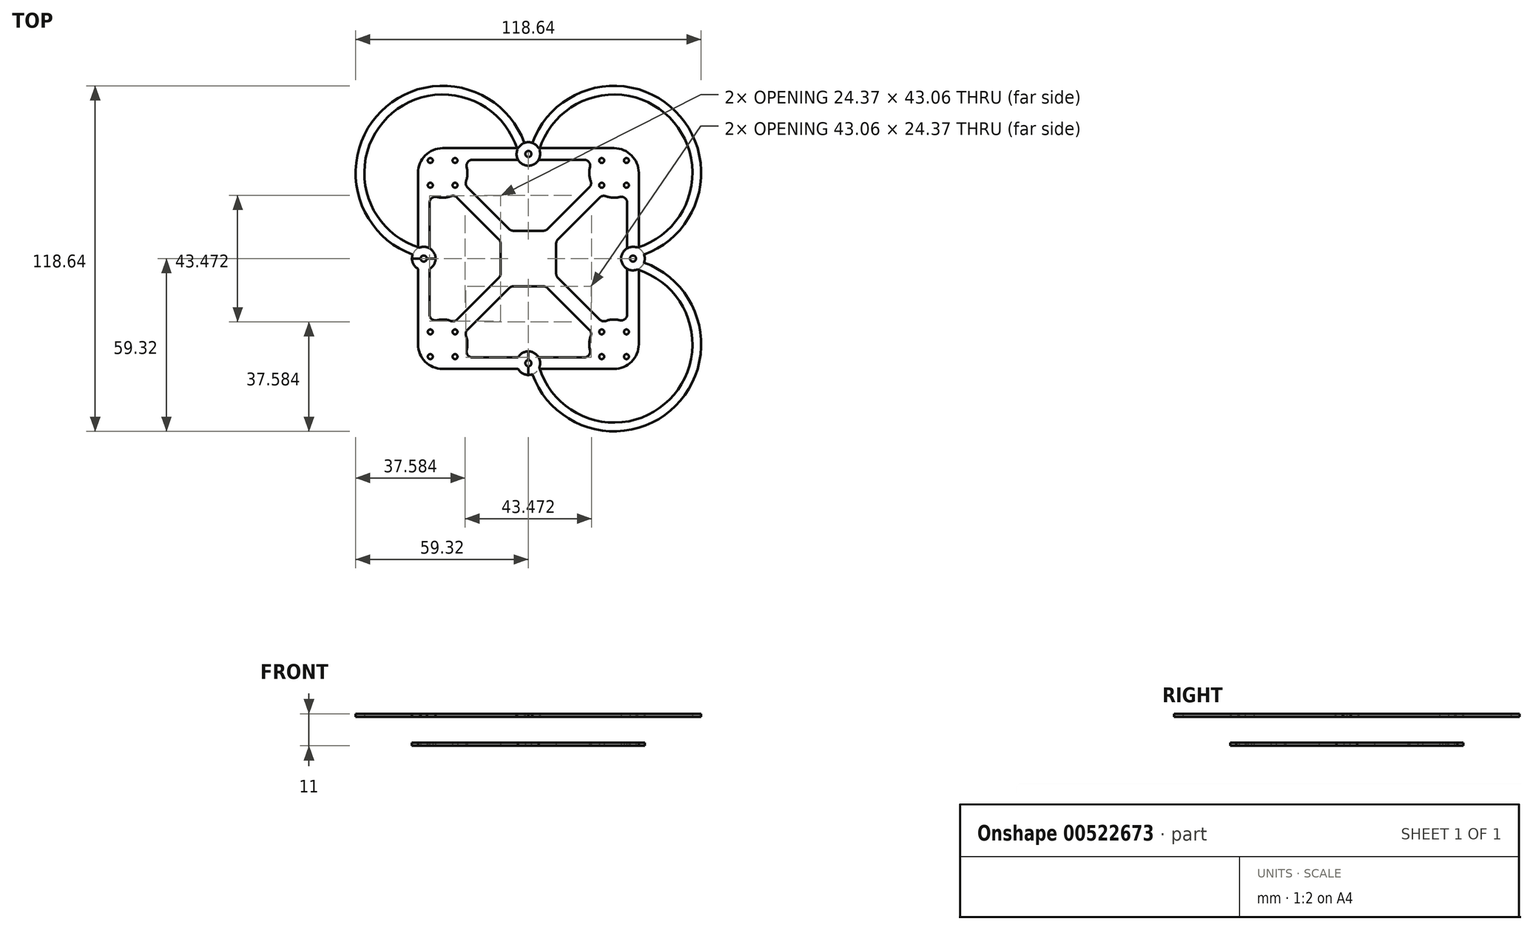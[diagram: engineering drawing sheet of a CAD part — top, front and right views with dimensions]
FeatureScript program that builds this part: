
annotation { "Feature Type Name" : "Feature", "Feature Type Description" : "" }
export const myFeature = defineFeature(function(context is Context, id is Id, definition is map)
    precondition{}
    {
        {
            var Q0;
            Q0=qCreatedBy(makeId("Top.planeOp"),FACE);
            var sketch = newSketch(context, id + "F0", { "sketchPlane" : qUnion([Q0])});
            skCircle(sketch, "E0", {"center": v(0, 0) * mm, "radius": 41.61 * mm, "construction": true});
            skCircle(sketch, "E1", {"center": v(29.42, 29.42) * mm, "radius": 25.4 * mm, "construction": true});
            skLineSegment(sketch, "E2", {"start": v(29.42, 29.42) * mm, "end": v(0, 0) * mm, "construction": true});
            skLineSegment(sketch, "E3", {"start": v(0, 0) * mm, "end": v(85.6, 0) * mm, "construction": true});
            skLineSegment(sketch, "E4", {"start": v(0, 0) * mm, "end": v(0, 79.54) * mm, "construction": true});
            skSolve(sketch);
        }
        {
            var Q0;
            Q0=qCreatedBy(makeId("Top.planeOp"),FACE);
            var sketch = newSketch(context, id + "F1", { "sketchPlane" : qUnion([Q0])});
            skCircle(sketch, "E5", {"center": v(29.42, 29.42) * mm, "radius": 8.5 * mm});
            skLineSegment(sketch, "E6", {"start": v(21.91, 25.45) * mm, "end": v(6.01, 9.55) * mm});
            skLineSegment(sketch, "E7", {"start": v(25.45, 21.91) * mm, "end": v(9.55, 6.01) * mm});
            skLineSegment(sketch, "E8", {"start": v(6.01, 9.55) * mm, "end": v(0, 9.55) * mm});
            skLineSegment(sketch, "E9", {"start": v(0, 9.55) * mm, "end": v(0, 0) * mm});
            skLineSegment(sketch, "E10", {"start": v(0, 0) * mm, "end": v(9.55, 0) * mm});
            skLineSegment(sketch, "E11", {"start": v(9.55, 0) * mm, "end": v(9.55, 6.01) * mm});
            skCircle(sketch, "E12", {"center": v(25.17, 25.17) * mm, "radius": 0.85 * mm});
            skCircle(sketch, "E13.1.0", {"center": v(33.67, 25.17) * mm, "radius": 0.85 * mm});
            skCircle(sketch, "E13.2.0", {"center": v(33.67, 33.67) * mm, "radius": 0.85 * mm});
            skCircle(sketch, "E13.3.0", {"center": v(25.17, 33.67) * mm, "radius": 0.85 * mm});
            skLineSegment(sketch, "E14.MirrorCS", {"start": v(22.21, 33.92) * mm, "end": v(3.52, 33.92) * mm});
            skLineSegment(sketch, "E15.MirrorCS", {"start": v(29.42, 37.92) * mm, "end": v(3.52, 37.92) * mm});
            skArc(sketch, "E16", {"start": v(0, 34.87) * mm, "mid": v(1.05, 35.92) * mm, "end": v(0, 36.97) * mm});
            skArc(sketch, "E17", {"start": v(0, 31.87) * mm, "mid": v(4.05, 35.92) * mm, "end": v(0, 39.97) * mm});
            skLineSegment(sketch, "E18", {"start": v(0, 31.87) * mm, "end": v(0, 34.87) * mm});
            skPoint(sketch, "E19.orphan", {"position": v(0, 29.97) * mm});
            skLineSegment(sketch, "E20.trimOffspring", {"start": v(0, 36.97) * mm, "end": v(0, 39.97) * mm});
            skPoint(sketch, "E21.MirrorP", {"position": v(29.97, 0) * mm});
            skLineSegment(sketch, "E22.MirrorCS", {"start": v(31.87, 0) * mm, "end": v(34.87, 0) * mm});
            skArc(sketch, "E23.MirrorCS", {"start": v(31.87, 0) * mm, "mid": v(35.92, 4.05) * mm, "end": v(39.97, 0) * mm});
            skArc(sketch, "E24.MirrorCS", {"start": v(34.87, 0) * mm, "mid": v(35.92, 1.05) * mm, "end": v(36.97, 0) * mm});
            skLineSegment(sketch, "E25.MirrorCS", {"start": v(33.92, 22.21) * mm, "end": v(33.92, 3.52) * mm});
            skLineSegment(sketch, "E26.MirrorCS", {"start": v(36.97, 0) * mm, "end": v(39.97, 0) * mm});
            skLineSegment(sketch, "E27.MirrorCS", {"start": v(37.92, 29.42) * mm, "end": v(37.92, 3.52) * mm});
            skSolve(sketch);
        }
        {
            var Q0;
            Q0 = qSketchRegion(id + "F1", true);
            extrude(context, id + "F2", {"entities" : qUnion([Q0]), "depth" : 1 * mm, "offsetDistance" : 25 * mm});
        }
        {
            var Q0;
            Q0=makeQuery(id+"F2.opExtrude","SWEPT_EDGE",EDGE,{"disambiguationData":[OSD([sQuery(id+"F1.wireOp",EDGE,"E5"),sQuery(id+"F1.wireOp",EDGE,"E25.MirrorCS")])]});
            var Q1;
            Q1=makeQuery(id+"F2.opExtrude","SWEPT_EDGE",EDGE,{"disambiguationData":[OSD([sQuery(id+"F1.wireOp",EDGE,"E5"),sQuery(id+"F1.wireOp",EDGE,"E7")])]});
            var Q2;
            Q2=makeQuery(id+"F2.opExtrude","SWEPT_EDGE",EDGE,{"disambiguationData":[OSD([sQuery(id+"F1.wireOp",EDGE,"E7"),sQuery(id+"F1.wireOp",EDGE,"E11")])]});
            var Q3;
            Q3=makeQuery(id+"F2.opExtrude","SWEPT_EDGE",EDGE,{"disambiguationData":[OSD([sQuery(id+"F1.wireOp",EDGE,"E6"),sQuery(id+"F1.wireOp",EDGE,"E8")])]});
            var Q4;
            Q4=makeQuery(id+"F2.opExtrude","SWEPT_EDGE",EDGE,{"disambiguationData":[OSD([sQuery(id+"F1.wireOp",EDGE,"E5"),sQuery(id+"F1.wireOp",EDGE,"E6")])]});
            var Q5;
            Q5=makeQuery(id+"F2.opExtrude","SWEPT_EDGE",EDGE,{"disambiguationData":[OSD([sQuery(id+"F1.wireOp",EDGE,"E5"),sQuery(id+"F1.wireOp",EDGE,"E14.MirrorCS")])]});
            fillet(context, id + "F3", {"entities" : qUnion([Q0, Q1, Q2, Q3, Q4, Q5]), "radius" : 2 * mm, "tangentPropagation" : true, "allowEdgeOverflow" : false});
        }
        {
            var Q0;
            Q0=makeQuery(id+"F2.opExtrude","SWEPT_BODY",BODY,{"disambiguationData":[OSD([sQuery(id+"F1.wireOp",EDGE,"E5"),sQuery(id+"F1.wireOp",EDGE,"E6"),sQuery(id+"F1.wireOp",EDGE,"E7"),sQuery(id+"F1.wireOp",EDGE,"E8"),sQuery(id+"F1.wireOp",EDGE,"E9"),sQuery(id+"F1.wireOp",EDGE,"E10"),sQuery(id+"F1.wireOp",EDGE,"E11"),sQuery(id+"F1.wireOp",EDGE,"1HwOaCKr-FHqW-oFPS-M7o7-vFpzogMrGbFQ"),sQuery(id+"F1.wireOp",EDGE,"fSPvFDCd-rED8-r1X3-aQF2-5EDJmj5I6fMv"),sQuery(id+"F1.wireOp",EDGE,"ag7oVWzA-YBNJ-l5QV-ecRD-Ys5e8jnzb400"),sQuery(id+"F1.wireOp",EDGE,"E12"),sQuery(id+"F1.wireOp",EDGE,"E13.1.0"),sQuery(id+"F1.wireOp",EDGE,"E13.2.0"),sQuery(id+"F1.wireOp",EDGE,"E13.3.0"),sQuery(id+"F1.wireOp",EDGE,"E14.MirrorCS"),sQuery(id+"F1.wireOp",EDGE,"E15.MirrorCS"),sQuery(id+"F1.wireOp",EDGE,"401848fb-c3c6-4292-853d-5288e9f784bb0.MirrorCS")])]});
            var Q1;
            Q1=makeQuery(id+"F2.opExtrude","SWEPT_FACE",FACE,{"disambiguationData":[OSD([sQuery(id+"F1.wireOp",EDGE,"E9")])]});
            mirror(context, id + "F4", {"operationType" : NewBodyOperationType.ADD, "entities" : qUnion([Q0]), "mirrorPlane" : qUnion([Q1])});
        }
        {
            var Q0;
            Q0=makeQuery(id+"F2.opExtrude","SWEPT_BODY",BODY,{"disambiguationData":[OSD([sQuery(id+"F1.wireOp",EDGE,"E5"),sQuery(id+"F1.wireOp",EDGE,"E6"),sQuery(id+"F1.wireOp",EDGE,"E7"),sQuery(id+"F1.wireOp",EDGE,"E8"),sQuery(id+"F1.wireOp",EDGE,"E9"),sQuery(id+"F1.wireOp",EDGE,"E10"),sQuery(id+"F1.wireOp",EDGE,"E11"),sQuery(id+"F1.wireOp",EDGE,"1HwOaCKr-FHqW-oFPS-M7o7-vFpzogMrGbFQ"),sQuery(id+"F1.wireOp",EDGE,"fSPvFDCd-rED8-r1X3-aQF2-5EDJmj5I6fMv"),sQuery(id+"F1.wireOp",EDGE,"ag7oVWzA-YBNJ-l5QV-ecRD-Ys5e8jnzb400"),sQuery(id+"F1.wireOp",EDGE,"E12"),sQuery(id+"F1.wireOp",EDGE,"E13.1.0"),sQuery(id+"F1.wireOp",EDGE,"E13.2.0"),sQuery(id+"F1.wireOp",EDGE,"E13.3.0"),sQuery(id+"F1.wireOp",EDGE,"E14.MirrorCS"),sQuery(id+"F1.wireOp",EDGE,"E15.MirrorCS"),sQuery(id+"F1.wireOp",EDGE,"401848fb-c3c6-4292-853d-5288e9f784bb0.MirrorCS")])]});
            var Q1;
            {var subQ0=makeQuery(id+"F2.opExtrude","SWEPT_FACE",FACE,{"disambiguationData":[OSD([sQuery(id+"F1.wireOp",EDGE,"E10")])]});Q1=makeQuery(id+"F4.boolean.opBoolean","MERGE",FACE,{"derivedFrom":[subQ0,makeQuery(id+"F4.opPattern","COPY",FACE,{"derivedFrom":subQ0,"instanceName":"1"})]});}
            mirror(context, id + "F5", {"operationType" : NewBodyOperationType.ADD, "entities" : qUnion([Q0]), "mirrorPlane" : qUnion([Q1])});
        }
        {
            var Q0;
            Q0=qCreatedBy(makeId("Top.planeOp"),FACE);
            var sketch = newSketch(context, id + "F6", { "sketchPlane" : qUnion([Q0])});
            skArc(sketch, "E28", {"start": v(37.45, 3.75) * mm, "mid": v(48.44, 48.44) * mm, "end": v(3.75, 37.45) * mm});
            skArc(sketch, "E29.0", {"start": v(39.74, 1.36) * mm, "mid": v(50.57, 50.57) * mm, "end": v(1.36, 39.74) * mm});
            skArc(sketch, "E30", {"start": v(36.97, 0) * mm, "mid": v(35.92, 1.05) * mm, "end": v(34.87, 0) * mm});
            skArc(sketch, "E31", {"start": v(39.97, 0) * mm, "mid": v(35.92, 4.05) * mm, "end": v(31.87, 0) * mm});
            skLineSegment(sketch, "E32", {"start": v(39.97, 0) * mm, "end": v(36.97, 0) * mm});
            skLineSegment(sketch, "E33.trimOffspring", {"start": v(34.87, 0) * mm, "end": v(31.87, 0) * mm});
            skArc(sketch, "E34", {"start": v(0, 34.87) * mm, "mid": v(1.05, 35.92) * mm, "end": v(0, 36.97) * mm});
            skArc(sketch, "E35", {"start": v(0, 31.87) * mm, "mid": v(4.05, 35.92) * mm, "end": v(0, 39.97) * mm});
            skLineSegment(sketch, "E36", {"start": v(0, 31.87) * mm, "end": v(0, 34.87) * mm});
            skLineSegment(sketch, "E37.trimOffspring", {"start": v(0, 36.97) * mm, "end": v(0, 39.97) * mm});
            skPoint(sketch, "E38.orphan", {"position": v(0, 31.18) * mm});
            skSolve(sketch);
        }
        {
            var Q0;
            Q0 = qSketchRegion(id + "F6", true);
            extrude(context, id + "F7", {"entities" : qUnion([Q0]), "depth" : 1 * mm, "offsetDistance" : 25 * mm});
        }
        {
            var Q0;
            Q0=makeQuery(id+"F7.opExtrude","SWEPT_BODY",BODY,{"disambiguationData":[OSD([sQuery(id+"F6.wireOp",EDGE,"E28"),sQuery(id+"F6.wireOp",EDGE,"E29.0"),sQuery(id+"F6.wireOp",EDGE,"E30"),sQuery(id+"F6.wireOp",EDGE,"E31"),sQuery(id+"F6.wireOp",EDGE,"E32"),sQuery(id+"F6.wireOp",EDGE,"E33.trimOffspring"),sQuery(id+"F6.wireOp",EDGE,"E34"),sQuery(id+"F6.wireOp",EDGE,"E35"),sQuery(id+"F6.wireOp",EDGE,"E36"),sQuery(id+"F6.wireOp",EDGE,"E37.trimOffspring")])]});
            var Q1;
            Q1=qCreatedBy(makeId("Top.planeOp"),FACE);
            transform(context, id + "F8", {"entities" : qUnion([Q0]), "transformType" : TransformType.TRANSLATION_DISTANCE, "transformDirection" : qUnion([Q1]), "distance" : 10 * mm, "makeCopy" : false});
        }
        {
            var Q0;
            Q0=makeQuery(id+"F7.opExtrude","SWEPT_BODY",BODY,{"disambiguationData":[OSD([sQuery(id+"F6.wireOp",EDGE,"E28"),sQuery(id+"F6.wireOp",EDGE,"E29.0"),sQuery(id+"F6.wireOp",EDGE,"E30"),sQuery(id+"F6.wireOp",EDGE,"E31"),sQuery(id+"F6.wireOp",EDGE,"E32"),sQuery(id+"F6.wireOp",EDGE,"E33.trimOffspring"),sQuery(id+"F6.wireOp",EDGE,"E34"),sQuery(id+"F6.wireOp",EDGE,"E35"),sQuery(id+"F6.wireOp",EDGE,"E36"),sQuery(id+"F6.wireOp",EDGE,"E37.trimOffspring")])]});
            var Q1;
            Q1=qCreatedBy(makeId("Right.planeOp"),FACE);
            mirror(context, id + "F9", {"operationType" : NewBodyOperationType.ADD, "entities" : qUnion([Q0]), "mirrorPlane" : qUnion([Q1])});
        }
        {
            var Q0;
            Q0=makeQuery(id+"F7.opExtrude","SWEPT_BODY",BODY,{"disambiguationData":[OSD([sQuery(id+"F6.wireOp",EDGE,"E28"),sQuery(id+"F6.wireOp",EDGE,"E29.0"),sQuery(id+"F6.wireOp",EDGE,"E30"),sQuery(id+"F6.wireOp",EDGE,"E31"),sQuery(id+"F6.wireOp",EDGE,"E32"),sQuery(id+"F6.wireOp",EDGE,"E33.trimOffspring"),sQuery(id+"F6.wireOp",EDGE,"E34"),sQuery(id+"F6.wireOp",EDGE,"E35"),sQuery(id+"F6.wireOp",EDGE,"E36"),sQuery(id+"F6.wireOp",EDGE,"E37.trimOffspring")])]});
            var Q1;
            Q1=qCreatedBy(makeId("Front.planeOp"),FACE);
            mirror(context, id + "F10", {"operationType" : NewBodyOperationType.ADD, "entities" : qUnion([Q0]), "mirrorPlane" : qUnion([Q1])});
        }
    });
